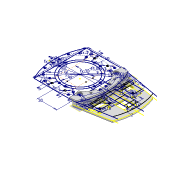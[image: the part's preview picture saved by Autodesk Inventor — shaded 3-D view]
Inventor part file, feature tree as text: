
AUTODESK INVENTOR PART (.ipt)
format: ipt  version: 2020.3 (Build 243373000, 373)  size: 268,800 bytes
history: native  units: mm
features: extrude x4, sketch x2, plane x1, fillet x1
ambient origin geometry x8: Origin, YZ Plane, XZ Plane, XY Plane, X Axis, Y Axis, Z Axis, Center Point
bodies: Solid1 (feature_tree)
feature tree (8):
  sketch  "Sketch1"  dims[d1=40.0mm d3=20.0mm d5=200.0mm d6=60.0mm d7=81.0mm d8=3.0mm d9=7.5mm d10=5.0mm d11=30.0mm d12=3.0mm d13=7.5mm d14=5.0mm d15=3.0mm d16=3.0mm d17=5.0mm d18=48.0mm d19=55.0mm d20=3.0mm d21=4.5mm d22=3.0mm d23=4.5mm d24=360.0deg d25=80.0mm d26=72.56mm d27=3.0mm d28=3.0mm d29=360.0deg d30=45.0deg d31=3.0mm d32=360.0deg d33=3.0mm d34=3.0mm d35=3.0mm d36=3.0mm d37=5.0mm]
  extrude  "Extrusion1"  Depth=5.0mm
  extrude  "Extrusion2"  Depth=2.0mm
  plane  "Work Plane1"
  sketch  "Sketch2"  dims[d38=5.0mm d39=30.0mm d40=40.5mm d41=14.0mm d42=18.0mm d43=19.0mm d44=14.0mm d45=7.0mm d46=2.0mm d47=2.0mm d48=2.0mm d49=2.0mm d50=2.0mm d51=2.0mm d52=7.0mm d53=2.5mm d54=2.5mm d55=2.0mm d56=2.0mm d57=2.5mm d58=2.0mm d59=2.0mm d60=35.0mm d61=16.0mm d62=4.0mm d63=4.0mm d64=22.0mm d65=14.0mm d66=13.962634mm d67=13.962634mm d68=2.0mm d69=4.0mm d70=2.0mm d71=0.0mm d72=4.0mm d73=0.0mm d74=1.5mm d75=2.5mm d76=0.0mm d77=2.0mm d78=6.5mm d79=6.5mm d80=1.25mm d81=0.0mm d82=0.5mm d83=0.872665mm]
  extrude  "Extrusion3"  Depth=2.0mm
  extrude  "Extrusion4"  Depth=2.0mm
  fillet  "Fillet1"  Radius=18.0mm
